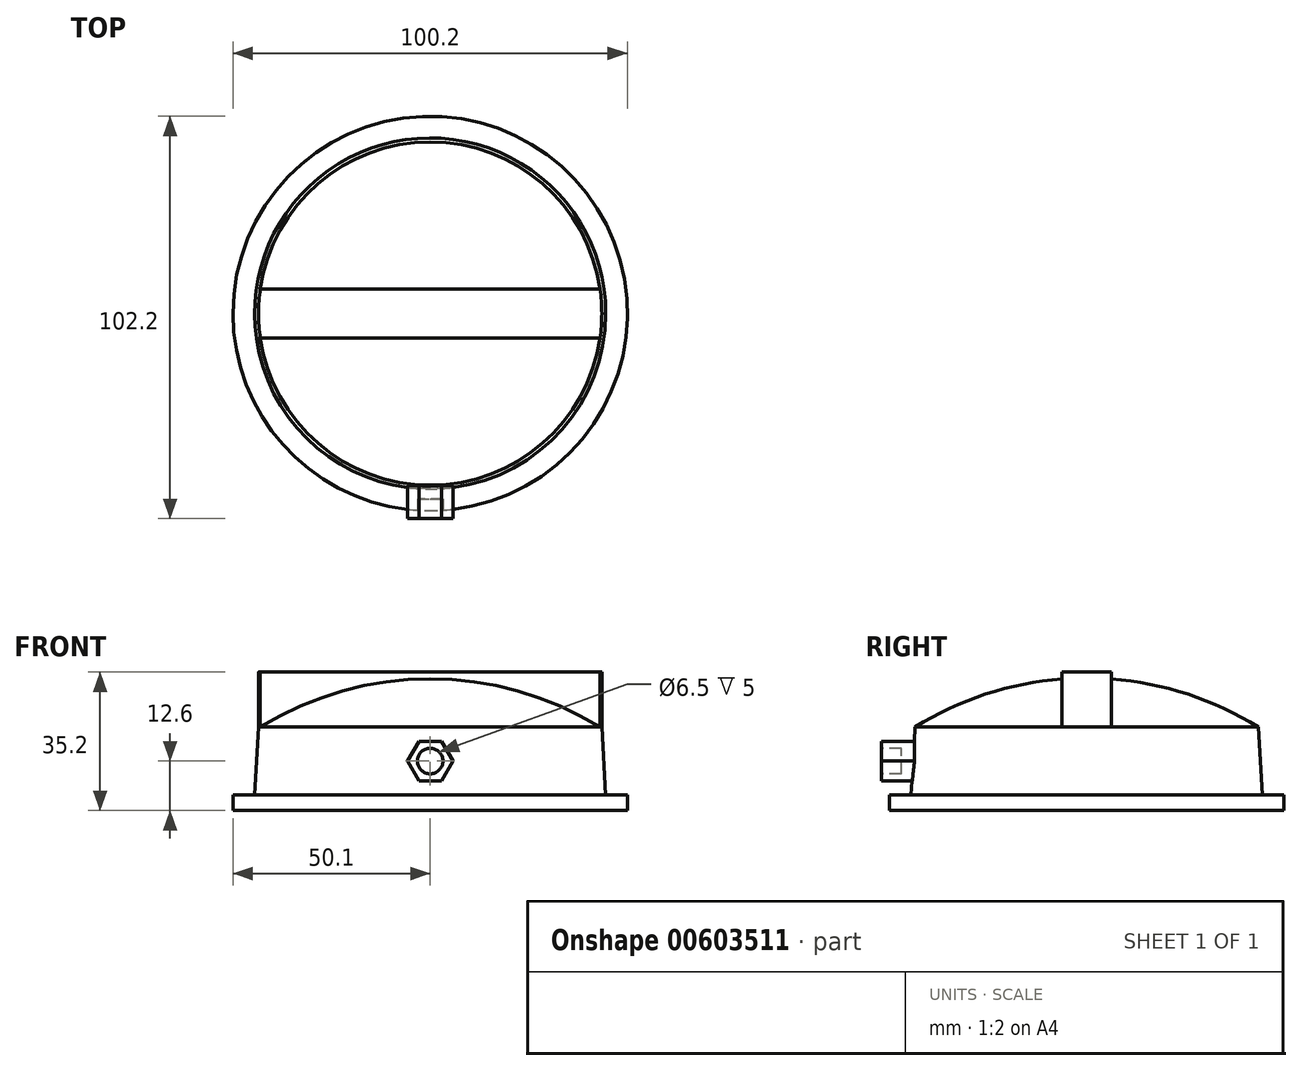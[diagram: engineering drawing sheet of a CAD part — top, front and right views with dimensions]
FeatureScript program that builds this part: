
annotation { "Feature Type Name" : "Feature", "Feature Type Description" : "" }
export const myFeature = defineFeature(function(context is Context, id is Id, definition is map)
    precondition{}
    {
        {
            var Q0;
            Q0=qCreatedBy(makeId("Top.planeOp"),FACE);
            var sketch = newSketch(context, id + "F0", { "sketchPlane" : qUnion([Q0])});
            skCircle(sketch, "E0", {"center": v(0, 0) * mm, "radius": 43.6 * mm});
            skSolve(sketch);
        }
        {
            var Q0;
            Q0=qCreatedBy(makeId("Top.planeOp"),FACE);
            cPlane(context, id + "F1", {"entities" : qUnion([Q0]), "cplaneType" : CPlaneType.OFFSET, "offset" : 17.2 * mm, "oppositeDirection" : true, "width" : 150 * mm, "height" : 150 * mm});
        }
        {
            var Q0;
            Q0=qCreatedBy(id+"F1.planeOp",FACE);
            var sketch = newSketch(context, id + "F2", { "sketchPlane" : qUnion([Q0])});
            skCircle(sketch, "E1.0", {"center": v(0, 0) * mm, "radius": 44.6 * mm});
            skSolve(sketch);
        }
        {
            var Q0;
            Q0=makeQuery(id+"F0.imprint","IMPRINT",FACE,{"disambiguationData":[TD([[makeQuery(id+"F0.imprint","IMPRINT",EDGE,{"derivedFrom":sQuery(id+"F0.wireOp",EDGE,"E0")}),1.0]])]});
            var Q1;
            Q1=makeQuery(id+"F2.imprint","IMPRINT",FACE,{"disambiguationData":[TD([[makeQuery(id+"F2.imprint","IMPRINT",EDGE,{"derivedFrom":sQuery(id+"F2.wireOp",EDGE,"E1.0")}),1.0]])]});
            loft(context, id + "F3", {"sheetProfilesArray" : [{ "sheetProfileEntities" : qUnion([Q0]) }, { "sheetProfileEntities" : qUnion([Q1]) }]});
        }
        {
            var Q0;
            Q0=makeQuery(id+"F3.opLoft","CAP_FACE",FACE,{"disambiguationData":[OSD([makeQuery(id+"F2.imprint","IMPRINT",FACE,{"disambiguationData":[TD([[makeQuery(id+"F2.imprint","IMPRINT",EDGE,{"derivedFrom":sQuery(id+"F2.wireOp",EDGE,"E1.0")}),1.0]])]})])],"isStart":true});
            var sketch = newSketch(context, id + "F4", { "sketchPlane" : qUnion([Q0])});
            skCircle(sketch, "E2.0", {"center": v(0, 0) * mm, "radius": 50.1 * mm});
            skSolve(sketch);
        }
        {
            var Q0;
            Q0=makeQuery(id+"F4.imprint","IMPRINT",FACE,{"disambiguationData":[TD([[makeQuery(id+"F4.imprint","IMPRINT",EDGE,{"derivedFrom":makeQuery(id+"F3.opLoft","MID_CAP_EDGE",EDGE,{"disambiguationData":[OSD([sQuery(id+"F0.wireOp",EDGE,"E0"),sQuery(id+"F2.wireOp",EDGE,"E1.0")])],"capPos":1.0})}),1.0]])]});
            var Q1;
            Q1=makeQuery(id+"F4.imprint","IMPRINT",FACE,{"disambiguationData":[TD([[makeQuery(id+"F4.imprint","IMPRINT",EDGE,{"derivedFrom":sQuery(id+"F4.wireOp",EDGE,"E2.0")}),1.0]])]});
            extrude(context, id + "F5", {"entities" : qUnion([Q0, Q1]), "operationType" : NewBodyOperationType.ADD, "depth" : 4 * mm, "offsetDistance" : 25 * mm});
        }
        {
            var Q0;
            Q0=qCreatedBy(makeId("Front.planeOp"),FACE);
            var sketch = newSketch(context, id + "F6", { "sketchPlane" : qUnion([Q0])});
            skLineSegment(sketch, "E3", {"start": v(0, 0) * mm, "end": v(0, 12.5) * mm});
            skLineSegment(sketch, "E4.0.0", {"start": v(-43.6, 0) * mm, "end": v(0, 0) * mm});
            skArc(sketch, "E5", {"start": v(0, 12.5) * mm, "mid": v(-22.68, 9.31) * mm, "end": v(-43.6, 0) * mm});
            skPoint(sketch, "E6.orphan", {"position": v(43.6, 0) * mm});
            skLineSegment(sketch, "E7", {"start": v(0, 0) * mm, "end": v(0, 23.42) * mm, "construction": true});
            skSolve(sketch);
        }
        {
            var Q0;
            Q0=makeQuery(id+"F6.imprint","IMPRINT",FACE,{"disambiguationData":[TD([[makeQuery(id+"F6.imprint","IMPRINT",EDGE,{"derivedFrom":sQuery(id+"F6.wireOp",EDGE,"E3")}),1.0]])]});
            var Q1;
            Q1=sQuery(id+"F6.wireOp",EDGE,"E7");
            revolve(context, id + "F7", {"operationType" : NewBodyOperationType.ADD, "entities" : qUnion([Q0]), "axis" : qUnion([Q1]), "revolveType" : RevolveType.FULL});
        }
        {
            var Q0;
            Q0=qCreatedBy(makeId("Top.planeOp"),FACE);
            cPlane(context, id + "F8", {"entities" : qUnion([Q0]), "cplaneType" : CPlaneType.OFFSET, "offset" : 14 * mm, "width" : 150 * mm, "height" : 150 * mm});
        }
        {
            var Q0;
            Q0=qCreatedBy(id+"F8.planeOp",FACE);
            var sketch = newSketch(context, id + "F9", { "sketchPlane" : qUnion([Q0])});
            skLineSegment(sketch, "E8.bottom", {"start": v(43.15, 6.25) * mm, "end": v(-43.15, 6.25) * mm});
            skLineSegment(sketch, "E8.top", {"start": v(43.15, -6.25) * mm, "end": v(-43.15, -6.25) * mm});
            skPoint(sketch, "E8.middle", {"position": v(0, 0) * mm});
            skCircle(sketch, "E9.0", {"center": v(0, 0) * mm, "radius": 43.6 * mm});
            skLineSegment(sketch, "E10", {"start": v(-43.15, 6.25) * mm, "end": v(43.15, -6.25) * mm, "construction": true});
            skLineSegment(sketch, "E11", {"start": v(43.15, 6.25) * mm, "end": v(-43.15, -6.25) * mm, "construction": true});
            skSolve(sketch);
        }
        {
            var Q0;
            {var subQ0=sQuery(id+"F9.wireOp",EDGE,"E8.bottom");Q0=makeQuery(id+"F9.imprint","IMPRINT",FACE,{"disambiguationData":[TD([[makeQuery(id+"F9.imprint","IMPRINT",EDGE,{"derivedFrom":subQ0}),1.0]])]});}
            extrude(context, id + "F10", {"entities" : qUnion([Q0]), "operationType" : NewBodyOperationType.ADD, "endBound" : BoundingType.UP_TO_NEXT, "oppositeDirection" : true, "depth" : 25 * mm, "offsetDistance" : 25 * mm});
        }
        {
            var Q0;
            Q0=qCreatedBy(makeId("Front.planeOp"),FACE);
            cPlane(context, id + "F11", {"entities" : qUnion([Q0]), "cplaneType" : CPlaneType.OFFSET, "offset" : (87.2 / 2) * mm, "width" : 150 * mm, "height" : 150 * mm});
        }
        {
            var Q0;
            Q0=qCreatedBy(id+"F11.planeOp",FACE);
            var sketch = newSketch(context, id + "F12", { "sketchPlane" : qUnion([Q0])});
            skCircle(sketch, "E12.cCircle", {"center": v(0, -8.6) * mm, "radius": 5 * mm, "construction": true});
            skLineSegment(sketch, "E12.0", {"start": v(5.77, -8.6) * mm, "end": v(2.89, -13.6) * mm});
            skLineSegment(sketch, "E12.1", {"start": v(2.89, -13.6) * mm, "end": v(-2.89, -13.6) * mm});
            skLineSegment(sketch, "E12.2", {"start": v(-2.89, -13.6) * mm, "end": v(-5.77, -8.6) * mm});
            skLineSegment(sketch, "E12.3", {"start": v(-5.77, -8.6) * mm, "end": v(-2.89, -3.6) * mm});
            skLineSegment(sketch, "E12.4", {"start": v(-2.89, -3.6) * mm, "end": v(2.89, -3.6) * mm});
            skLineSegment(sketch, "E12.5", {"start": v(2.89, -3.6) * mm, "end": v(5.77, -8.6) * mm});
            skPoint(sketch, "E12.0.midPoint", {"position": v(4.33, -11.1) * mm});
            skLineSegment(sketch, "E13.0", {"start": v(43.15, 0) * mm, "end": v(-43.15, 0) * mm, "construction": true});
            skLineSegment(sketch, "E14.0", {"start": v(50.1, -17.2) * mm, "end": v(-50.1, -17.2) * mm, "construction": true});
            skLineSegment(sketch, "E15", {"start": v(0, 0) * mm, "end": v(0, -17.2) * mm, "construction": true});
            skSolve(sketch);
        }
        {
            var Q0;
            Q0 = qSketchRegion(id + "F12", true);
            extrude(context, id + "F13", {"entities" : qUnion([Q0]), "operationType" : NewBodyOperationType.ADD, "depth" : 8.5 * mm, "offsetDistance" : 25 * mm});
        }
        {
            var Q0;
            Q0=makeQuery(id+"F13.opExtrude","CAP_FACE",FACE,{"disambiguationData":[OSD([sQuery(id+"F12.wireOp",EDGE,"E12.0"),sQuery(id+"F12.wireOp",EDGE,"E12.1"),sQuery(id+"F12.wireOp",EDGE,"E12.2"),sQuery(id+"F12.wireOp",EDGE,"E12.3"),sQuery(id+"F12.wireOp",EDGE,"E12.4"),sQuery(id+"F12.wireOp",EDGE,"E12.5")])],"isStart":false});
            var sketch = newSketch(context, id + "F14", { "sketchPlane" : qUnion([Q0])});
            skCircle(sketch, "E16", {"center": v(0, -8.6) * mm, "radius": 3.25 * mm});
            skSolve(sketch);
        }
        {
            var Q0;
            Q0=makeQuery(id+"F14.imprint","IMPRINT",FACE,{"disambiguationData":[TD([[makeQuery(id+"F14.imprint","IMPRINT",EDGE,{"derivedFrom":sQuery(id+"F14.wireOp",EDGE,"E16")}),1.0]])]});
            extrude(context, id + "F15", {"entities" : qUnion([Q0]), "operationType" : NewBodyOperationType.REMOVE, "oppositeDirection" : true, "depth" : 5 * mm, "offsetDistance" : 25 * mm});
        }
    });
